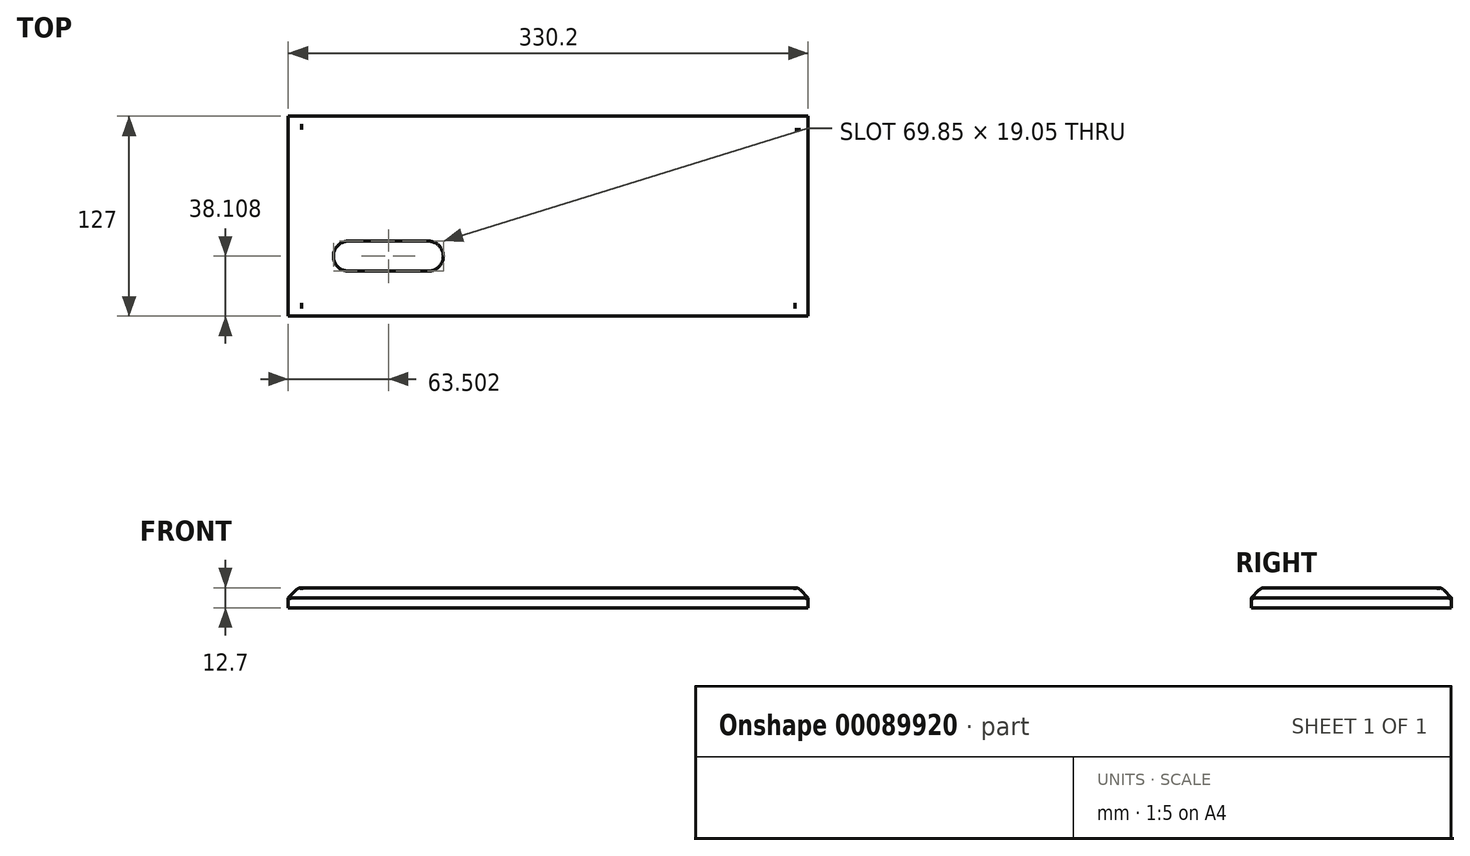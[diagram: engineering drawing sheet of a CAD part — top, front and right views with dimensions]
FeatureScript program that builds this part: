
annotation { "Feature Type Name" : "Feature", "Feature Type Description" : "" }
export const myFeature = defineFeature(function(context is Context, id is Id, definition is map)
    precondition{}
    {
        {
            var Q0;
            Q0=qCreatedBy(makeId("Top.planeOp"),FACE);
            var sketch = newSketch(context, id + "F0", { "sketchPlane" : qUnion([Q0])});
            skLineSegment(sketch, "E0.bottom", {"start": v(-187.33, -98.39) * mm, "end": v(142.87, -98.39) * mm});
            skLineSegment(sketch, "E0.top", {"start": v(-187.33, 28.61) * mm, "end": v(142.87, 28.61) * mm});
            skLineSegment(sketch, "E0.left", {"start": v(-187.33, -98.39) * mm, "end": v(-187.33, 28.61) * mm});
            skLineSegment(sketch, "E0.right", {"start": v(142.87, -98.39) * mm, "end": v(142.87, 28.61) * mm});
            skSolve(sketch);
        }
        {
            var Q0;
            Q0 = qSketchRegion(id + "F0", true);
            extrude(context, id + "F1", {"entities" : qUnion([Q0]), "depth" : 12.7 * mm});
        }
        {
            var Q0;
            Q0=makeQuery(id+"F1.opExtrude","CAP_FACE",FACE,{"disambiguationData":[OSD([sQuery(id+"F0.wireOp",EDGE,"E0.bottom"),sQuery(id+"F0.wireOp",EDGE,"E0.top"),sQuery(id+"F0.wireOp",EDGE,"E0.left"),sQuery(id+"F0.wireOp",EDGE,"E0.right")])],"isStart":false});
            var sketch = newSketch(context, id + "F2", { "sketchPlane" : qUnion([Q0])});
            skArc(sketch, "E1", {"start": v(-149.21, -50.76) * mm, "mid": v(-158.75, -60.46) * mm, "end": v(-148.87, -69.8) * mm});
            skArc(sketch, "E2", {"start": v(-98.43, -69.8) * mm, "mid": v(-88.9, -60.28) * mm, "end": v(-98.43, -50.76) * mm});
            skLineSegment(sketch, "E3", {"start": v(-149.21, -50.76) * mm, "end": v(-98.43, -50.76) * mm});
            skLineSegment(sketch, "E4", {"start": v(-149.59, -69.8) * mm, "end": v(-98.43, -69.8) * mm});
            skSolve(sketch);
        }
        {
            var Q0;
            Q0 = qSketchRegion(id + "F2", true);
            extrude(context, id + "F3", {"entities" : qUnion([Q0]), "operationType" : NewBodyOperationType.REMOVE, "endBound" : BoundingType.THROUGH_ALL, "oppositeDirection" : true, "depth" : 25.4 * mm});
        }
        {
            var Q0;
            Q0=makeQuery(id+"F1.opExtrude","CAP_EDGE",EDGE,{"disambiguationData":[OSD([sQuery(id+"F0.wireOp",EDGE,"E0.left")])],"isStart":false});
            var Q1;
            Q1=makeQuery(id+"F1.opExtrude","CAP_EDGE",EDGE,{"disambiguationData":[OSD([sQuery(id+"F0.wireOp",EDGE,"E0.bottom")])],"isStart":false});
            var Q2;
            Q2=makeQuery(id+"F1.opExtrude","CAP_EDGE",EDGE,{"disambiguationData":[OSD([sQuery(id+"F0.wireOp",EDGE,"E0.top")])],"isStart":false});
            var Q3;
            Q3=makeQuery(id+"F1.opExtrude","CAP_EDGE",EDGE,{"disambiguationData":[OSD([sQuery(id+"F0.wireOp",EDGE,"E0.right")])],"isStart":false});
            chamfer(context, id + "F4", {"entities" : qUnion([Q0, Q1, Q2, Q3]), "width" : 6.35 * mm, "tangentPropagation" : true});
        }
        {
            var Q0;
            {var subQ0=sQuery(id+"F0.wireOp",EDGE,"E0.bottom");Q0=makeQuery(id+"F4.opChamfer","BLEND_EDGE",EDGE,{"blendedFrom":[makeQuery(id+"F1.opExtrude","CAP_EDGE",EDGE,{"disambiguationData":[OSD([subQ0])],"isStart":false}),makeQuery(id+"F1.opExtrude","CAP_FACE",FACE,{"disambiguationData":[OSD([subQ0,sQuery(id+"F0.wireOp",EDGE,"E0.top"),sQuery(id+"F0.wireOp",EDGE,"E0.left"),sQuery(id+"F0.wireOp",EDGE,"E0.right")])],"isStart":false})],"blendedInto":[makeQuery(id+"F1.opExtrude","CAP_FACE",FACE,{"disambiguationData":[OSD([subQ0,sQuery(id+"F0.wireOp",EDGE,"E0.top"),sQuery(id+"F0.wireOp",EDGE,"E0.left"),sQuery(id+"F0.wireOp",EDGE,"E0.right")])],"isStart":false})]});}
            fillet(context, id + "F5", {"entities" : qUnion([Q0]), "radius" : 5.08 * mm, "tangentPropagation" : true, "allowEdgeOverflow" : false});
        }
        {
            var Q0;
            {var subQ0=sQuery(id+"F0.wireOp",EDGE,"E0.right");Q0=makeQuery(id+"F4.opChamfer","BLEND_EDGE",EDGE,{"blendedFrom":[makeQuery(id+"F1.opExtrude","CAP_EDGE",EDGE,{"disambiguationData":[OSD([subQ0])],"isStart":false}),makeQuery(id+"F1.opExtrude","CAP_FACE",FACE,{"disambiguationData":[OSD([sQuery(id+"F0.wireOp",EDGE,"E0.bottom"),sQuery(id+"F0.wireOp",EDGE,"E0.top"),sQuery(id+"F0.wireOp",EDGE,"E0.left"),subQ0])],"isStart":false})],"blendedInto":[makeQuery(id+"F1.opExtrude","CAP_FACE",FACE,{"disambiguationData":[OSD([sQuery(id+"F0.wireOp",EDGE,"E0.bottom"),sQuery(id+"F0.wireOp",EDGE,"E0.top"),sQuery(id+"F0.wireOp",EDGE,"E0.left"),subQ0])],"isStart":false})]});}
            fillet(context, id + "F6", {"entities" : qUnion([Q0]), "radius" : 5.08 * mm, "tangentPropagation" : true, "allowEdgeOverflow" : false});
        }
        {
            var Q0;
            {var subQ0=sQuery(id+"F0.wireOp",EDGE,"E0.top");Q0=makeQuery(id+"F4.opChamfer","BLEND_EDGE",EDGE,{"blendedFrom":[makeQuery(id+"F1.opExtrude","CAP_EDGE",EDGE,{"disambiguationData":[OSD([subQ0])],"isStart":false}),makeQuery(id+"F1.opExtrude","CAP_FACE",FACE,{"disambiguationData":[OSD([sQuery(id+"F0.wireOp",EDGE,"E0.bottom"),subQ0,sQuery(id+"F0.wireOp",EDGE,"E0.left"),sQuery(id+"F0.wireOp",EDGE,"E0.right")])],"isStart":false})],"blendedInto":[makeQuery(id+"F1.opExtrude","CAP_FACE",FACE,{"disambiguationData":[OSD([sQuery(id+"F0.wireOp",EDGE,"E0.bottom"),subQ0,sQuery(id+"F0.wireOp",EDGE,"E0.left"),sQuery(id+"F0.wireOp",EDGE,"E0.right")])],"isStart":false})]});}
            fillet(context, id + "F7", {"entities" : qUnion([Q0]), "radius" : 5.08 * mm, "tangentPropagation" : true, "allowEdgeOverflow" : false});
        }
        {
            var Q0;
            {var subQ0=sQuery(id+"F0.wireOp",EDGE,"E0.left");Q0=makeQuery(id+"F4.opChamfer","BLEND_EDGE",EDGE,{"blendedFrom":[makeQuery(id+"F1.opExtrude","CAP_EDGE",EDGE,{"disambiguationData":[OSD([subQ0])],"isStart":false}),makeQuery(id+"F1.opExtrude","CAP_FACE",FACE,{"disambiguationData":[OSD([sQuery(id+"F0.wireOp",EDGE,"E0.bottom"),sQuery(id+"F0.wireOp",EDGE,"E0.top"),subQ0,sQuery(id+"F0.wireOp",EDGE,"E0.right")])],"isStart":false})],"blendedInto":[makeQuery(id+"F1.opExtrude","CAP_FACE",FACE,{"disambiguationData":[OSD([sQuery(id+"F0.wireOp",EDGE,"E0.bottom"),sQuery(id+"F0.wireOp",EDGE,"E0.top"),subQ0,sQuery(id+"F0.wireOp",EDGE,"E0.right")])],"isStart":false})]});}
            fillet(context, id + "F8", {"entities" : qUnion([Q0]), "radius" : 5.08 * mm, "tangentPropagation" : true, "allowEdgeOverflow" : false});
        }
    });
